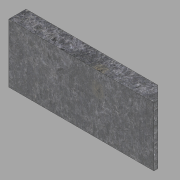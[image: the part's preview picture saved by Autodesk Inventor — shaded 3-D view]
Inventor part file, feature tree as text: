
AUTODESK INVENTOR PART (.ipt)
format: ipt  version: 2022.2 (Build 262287000, 287)  size: 143,360 bytes
history: native  units: in
note: dims shown in document units (in); Inventor stores cm internally (conversion verified against a paired STEP export)
features: extrude x4, sketch x4, thicken_offset x1
ambient origin geometry x8: Origin, YZ Plane, XZ Plane, XY Plane, X Axis, Y Axis, Z Axis, Center Point
bodies: Solid1 (feature_tree)
feature tree (9):
  extrude  "Extrusion1"  Depth=7.625in
  extrude  "Extrusion3"  Depth=18.8125in TaperAngle=0.0deg
  thicken_offset  "Thicken1"
  extrude  "Extrusion4"  Depth=0.125in
  extrude  "Extrusion5"  Depth=7.625in
  sketch  "Sketch1"  dims[d0=2.25in d1=7.625in]
  sketch  "Sketch3"  dims[d2=18.8125in d3=0.0in d10=1.0in d11=0.0in]
  sketch  "Sketch4"  dims[d12=0.125in d13=0.125in]
  sketch  "Sketch6"  dims[d15=7.625in d16=0.0in d17=0.5in d18=0.6765in d19=0.0in]
